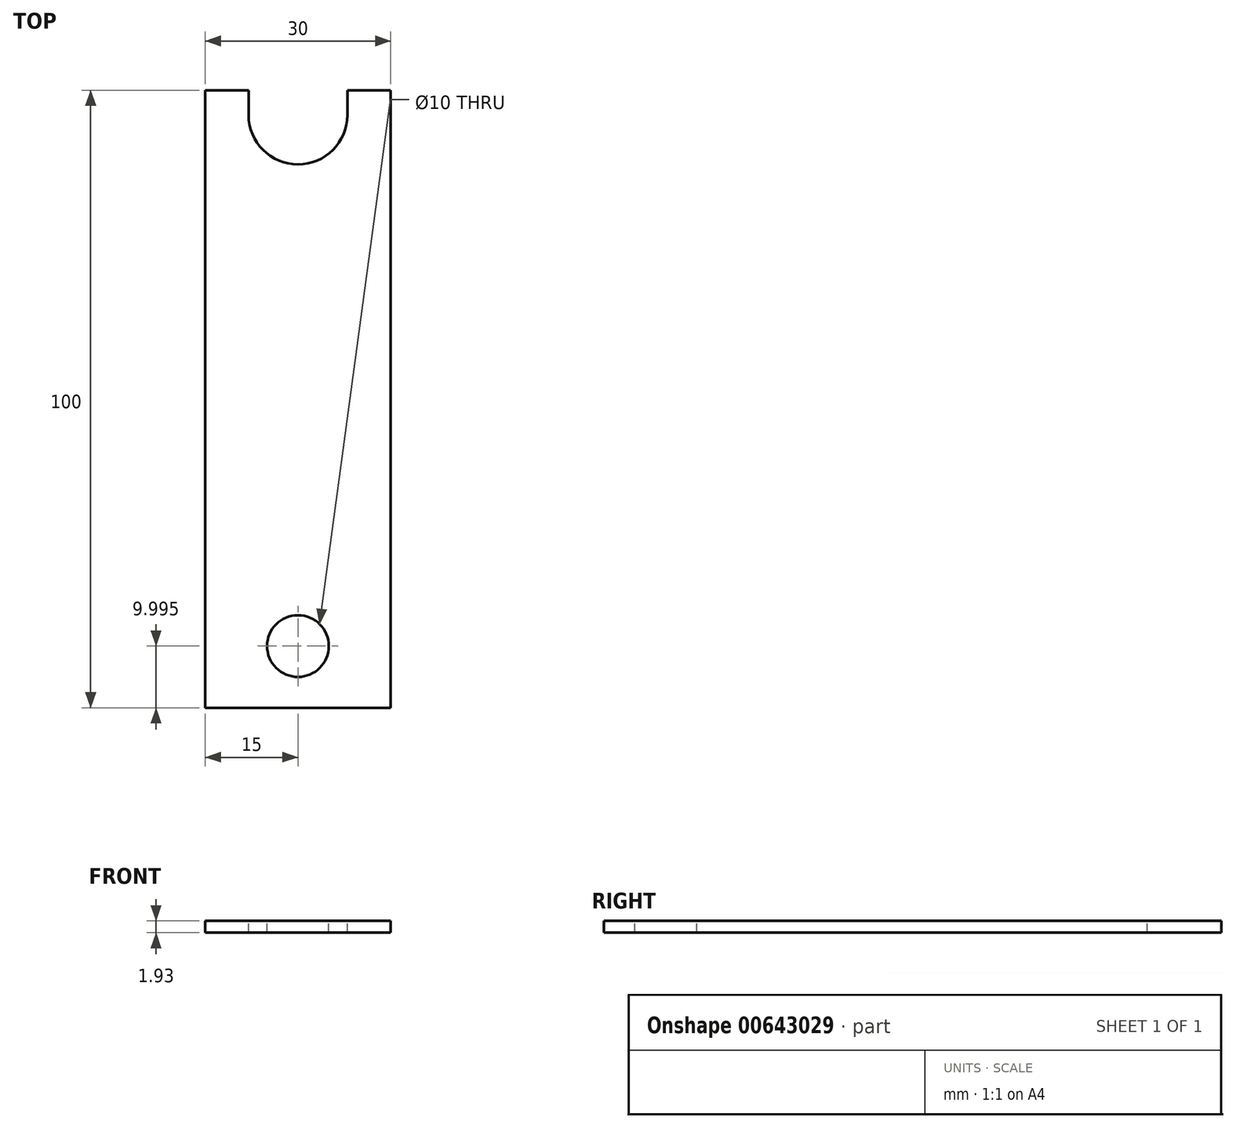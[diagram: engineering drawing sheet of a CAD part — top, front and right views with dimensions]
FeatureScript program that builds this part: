
annotation { "Feature Type Name" : "Feature", "Feature Type Description" : "" }
export const myFeature = defineFeature(function(context is Context, id is Id, definition is map)
    precondition{}
    {
        {
            var Q0;
            Q0=qCreatedBy(makeId("Top.planeOp"),FACE);
            var sketch = newSketch(context, id + "F0", { "sketchPlane" : qUnion([Q0])});
            skLineSegment(sketch, "E0.bottom", {"start": v(-6.54, 53.67) * mm, "end": v(23.46, 53.67) * mm});
            skLineSegment(sketch, "E0.top", {"start": v(-6.54, -46.33) * mm, "end": v(23.46, -46.33) * mm});
            skLineSegment(sketch, "E0.left", {"start": v(-6.54, 53.67) * mm, "end": v(-6.54, -46.33) * mm});
            skLineSegment(sketch, "E0.right", {"start": v(23.46, 53.67) * mm, "end": v(23.46, -46.33) * mm});
            skSolve(sketch);
        }
        {
            var Q0;
            Q0=makeQuery(id+"F0.imprint","IMPRINT",FACE,{"disambiguationData":[TD([[makeQuery(id+"F0.imprint","IMPRINT",EDGE,{"derivedFrom":sQuery(id+"F0.wireOp",EDGE,"E0.bottom")}),-1.0]])]});
            extrude(context, id + "F1", {"entities" : qUnion([Q0]), "depth" : 1.93 * mm, "offsetDistance" : 25 * mm});
        }
        {
            var Q0;
            Q0=makeQuery(id+"F1.opExtrude","CAP_FACE",FACE,{"disambiguationData":[OSD([sQuery(id+"F0.wireOp",EDGE,"E0.bottom"),sQuery(id+"F0.wireOp",EDGE,"E0.top"),sQuery(id+"F0.wireOp",EDGE,"E0.left"),sQuery(id+"F0.wireOp",EDGE,"E0.right")])],"isStart":false});
            var sketch = newSketch(context, id + "F2", { "sketchPlane" : qUnion([Q0])});
            skPoint(sketch, "E1", {"position": v(8.46, 49.67) * mm});
            skPoint(sketch, "E2", {"position": v(8.46, -36.33) * mm});
            skArc(sketch, "E3", {"start": v(0.46, 49.67) * mm, "mid": v(8.46, 41.67) * mm, "end": v(16.46, 49.67) * mm});
            skLineSegment(sketch, "E4", {"start": v(0.46, 49.67) * mm, "end": v(0.46, 53.67) * mm});
            skLineSegment(sketch, "E5", {"start": v(16.46, 49.67) * mm, "end": v(16.46, 53.67) * mm});
            skSolve(sketch);
        }
        {
            var Q0;
            Q0=sQuery(id+"F2.wireOp",VERTEX,"E2");
            var Q1;
            Q1=makeQuery(id+"F1.opExtrude","SWEPT_BODY",BODY,{"disambiguationData":[OSD([sQuery(id+"F0.wireOp",EDGE,"E0.bottom"),sQuery(id+"F0.wireOp",EDGE,"E0.top"),sQuery(id+"F0.wireOp",EDGE,"E0.left"),sQuery(id+"F0.wireOp",EDGE,"E0.right")])]});
            hole(context, id + "F3", {"style" : HoleStyle.SIMPLE, "endStyle" : HoleEndStyle.THROUGH, "holeDiameter" : 10 * mm, "majorDiameter" : 5 * mm, "isTappedThrough" : true, "tappedDepth" : 17.9 * mm, "tapClearance" : 3, "locations" : qUnion([Q0]), "scope" : qUnion([Q1])});
        }
        {
            var Q0;
            Q0 = qSketchRegion(id + "F5arhABHyNt6lxX_1", true);
            var Q1;
            Q1=makeQuery(id+"F2.imprint","IMPRINT",FACE,{"disambiguationData":[TD([[makeQuery(id+"F2.imprint","IMPRINT",EDGE,{"derivedFrom":sQuery(id+"F2.wireOp",EDGE,"E3")}),1.0]])]});
            extrude(context, id + "F4", {"entities" : qUnion([Q0, Q1]), "operationType" : NewBodyOperationType.REMOVE, "oppositeDirection" : true, "depth" : 1.93 * mm, "offsetDistance" : 25 * mm});
        }
    });
